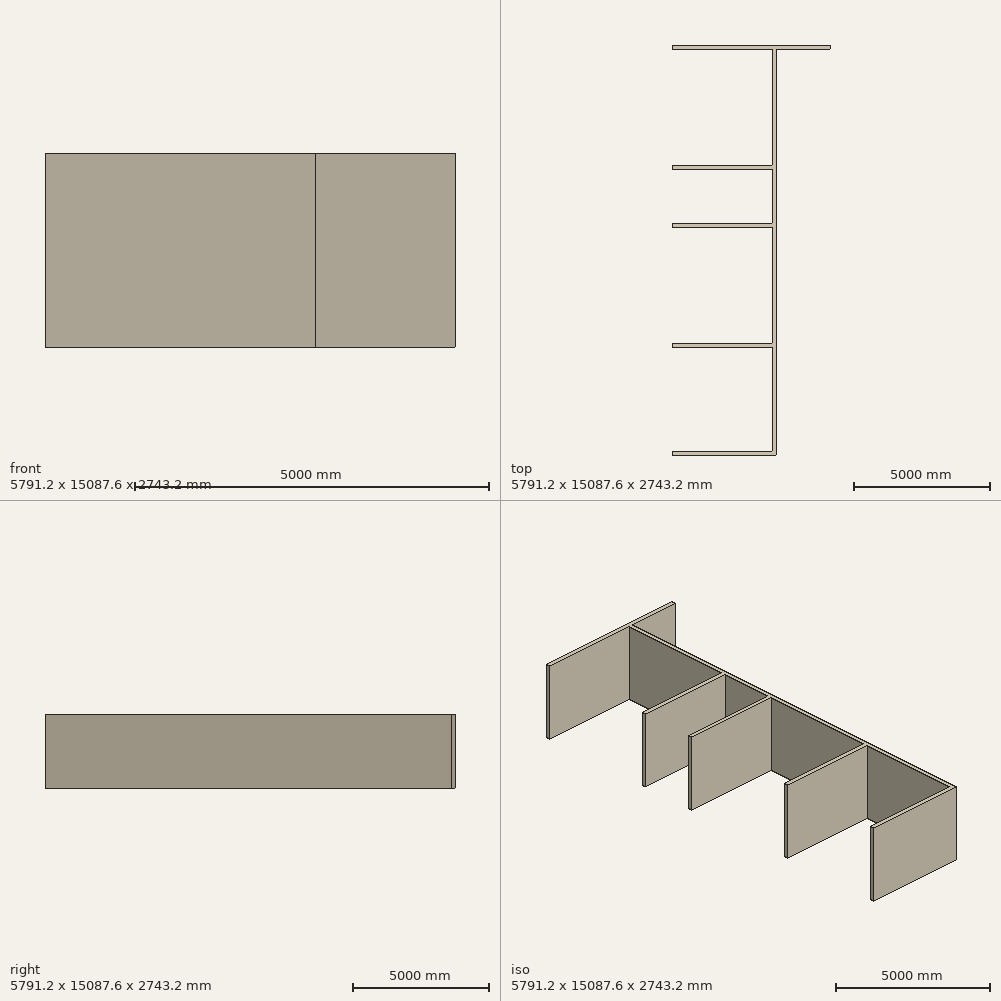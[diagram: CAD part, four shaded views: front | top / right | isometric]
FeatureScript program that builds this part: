
annotation { "Feature Type Name" : "Feature", "Feature Type Description" : "" }
export const myFeature = defineFeature(function(context is Context, id is Id, definition is map)
    precondition{}
    {
        {
            var Q0;
            Q0=qCreatedBy(makeId("Top.planeOp"),FACE);
            var sketch = newSketch(context, id + "F0", { "sketchPlane" : qUnion([Q0])});
            skLineSegment(sketch, "E0.bottom", {"start": v(0, 0) * mm, "end": v(-1981.2, 0) * mm});
            skLineSegment(sketch, "E0.top", {"start": v(0, 152.4) * mm, "end": v(-5791.2, 152.4) * mm});
            skLineSegment(sketch, "E0.left", {"start": v(0, 0) * mm, "end": v(0, 152.4) * mm});
            skLineSegment(sketch, "E0.right", {"start": v(-5791.2, 0) * mm, "end": v(-5791.2, 152.4) * mm});
            skLineSegment(sketch, "E1.left", {"start": v(-2133.6, 0) * mm, "end": v(-2133.6, -14782.8) * mm});
            skLineSegment(sketch, "E1.right", {"start": v(-1981.2, 0) * mm, "end": v(-1981.2, -14935.2) * mm});
            skLineSegment(sketch, "E2.trimOffspring", {"start": v(-2133.6, 0) * mm, "end": v(-5791.2, 0) * mm});
            skLineSegment(sketch, "E3.bottom", {"start": v(-5791.2, -4267.2) * mm, "end": v(-2133.6, -4267.2) * mm});
            skLineSegment(sketch, "E3.top", {"start": v(-5791.2, -4419.6) * mm, "end": v(-2133.6, -4419.6) * mm});
            skLineSegment(sketch, "E3.left", {"start": v(-5791.2, -4267.2) * mm, "end": v(-5791.2, -4419.6) * mm});
            skLineSegment(sketch, "E3.right", {"start": v(-2133.6, -4267.2) * mm, "end": v(-2133.6, -4419.6) * mm});
            skLineSegment(sketch, "E4.bottom", {"start": v(-5791.2, -6400.8) * mm, "end": v(-2133.6, -6400.8) * mm});
            skLineSegment(sketch, "E4.top", {"start": v(-5791.2, -6553.2) * mm, "end": v(-2133.6, -6553.2) * mm});
            skLineSegment(sketch, "E4.left", {"start": v(-5791.2, -6400.8) * mm, "end": v(-5791.2, -6553.2) * mm});
            skLineSegment(sketch, "E4.right", {"start": v(-2133.6, -6400.8) * mm, "end": v(-2133.6, -6553.2) * mm});
            skLineSegment(sketch, "E5.bottom", {"start": v(-5791.2, -10820.4) * mm, "end": v(-2133.6, -10820.4) * mm});
            skLineSegment(sketch, "E5.top", {"start": v(-5791.2, -10972.8) * mm, "end": v(-2133.6, -10972.8) * mm});
            skLineSegment(sketch, "E5.left", {"start": v(-5791.2, -10820.4) * mm, "end": v(-5791.2, -10972.8) * mm});
            skLineSegment(sketch, "E5.right", {"start": v(-2133.6, -10820.4) * mm, "end": v(-2133.6, -10972.8) * mm});
            skLineSegment(sketch, "E6.bottom", {"start": v(-5791.2, -14782.8) * mm, "end": v(-2133.6, -14782.8) * mm});
            skLineSegment(sketch, "E6.top", {"start": v(-5791.2, -14935.2) * mm, "end": v(-1981.2, -14935.2) * mm});
            skLineSegment(sketch, "E6.left", {"start": v(-5791.2, -14782.8) * mm, "end": v(-5791.2, -14935.2) * mm});
            skSolve(sketch);
        }
        {
            var Q0;
            Q0 = qSketchRegion(id + "F0", true);
            extrude(context, id + "F1", {"entities" : qUnion([Q0]), "depth" : 2743.2 * mm});
        }
    });
